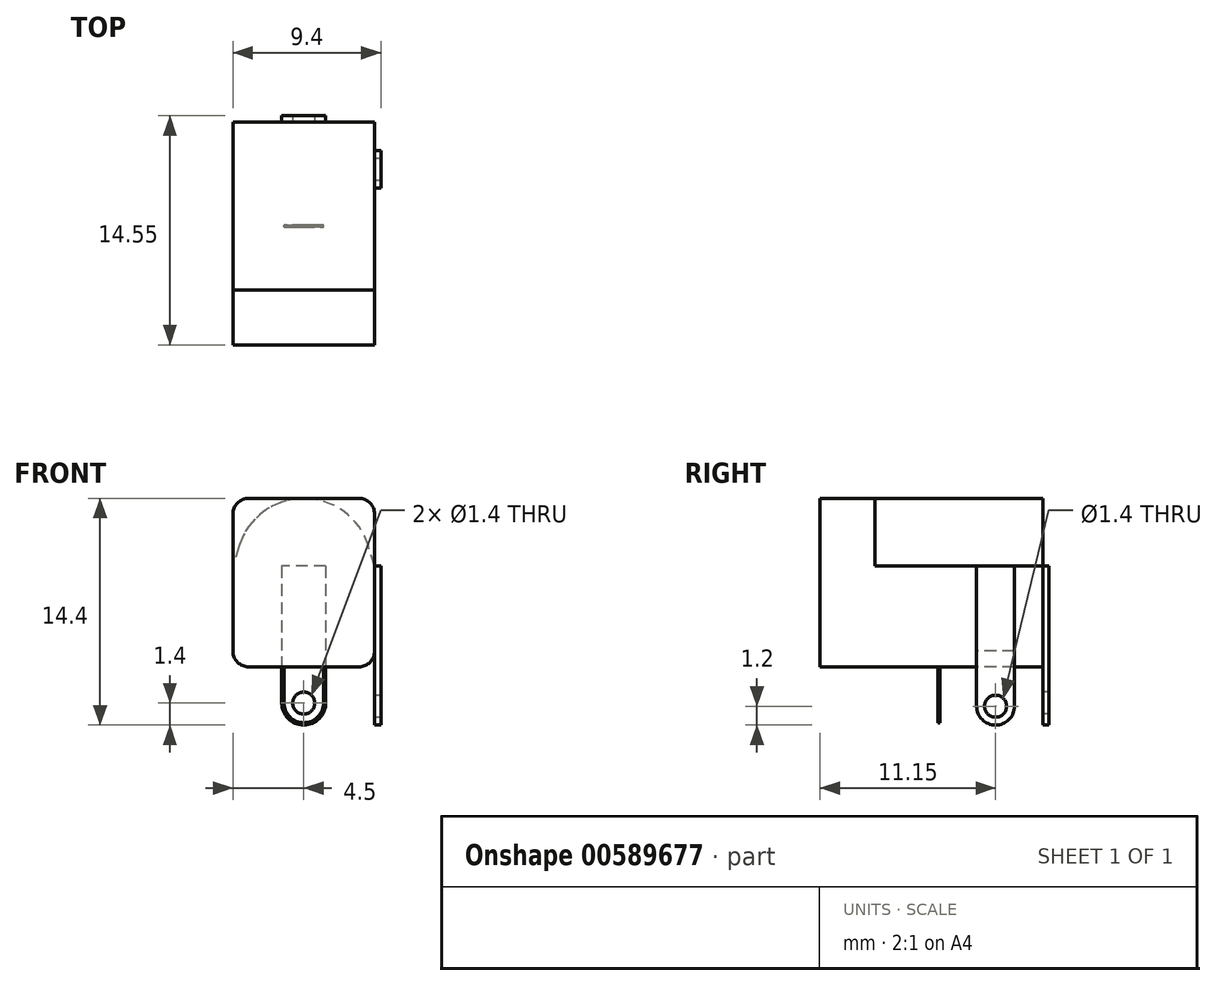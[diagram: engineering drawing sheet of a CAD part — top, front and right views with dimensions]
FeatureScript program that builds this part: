
annotation { "Feature Type Name" : "Feature", "Feature Type Description" : "" }
export const myFeature = defineFeature(function(context is Context, id is Id, definition is map)
    precondition{}
    {
        {
            var Q0;
            Q0=qCreatedBy(makeId("Front.planeOp"),FACE);
            var sketch = newSketch(context, id + "F0", { "sketchPlane" : qUnion([Q0])});
            skArc(sketch, "E0", {"start": v(-4.1, 1.27) * mm, "mid": v(0, 4.3) * mm, "end": v(4.1, 1.27) * mm});
            skLineSegment(sketch, "E1", {"start": v(-4.5, 0) * mm, "end": v(-4.5, -6.4) * mm});
            skLineSegment(sketch, "E2", {"start": v(4.5, -6.4) * mm, "end": v(4.5, 0) * mm});
            skLineSegment(sketch, "E3", {"start": v(-4.5, -6.4) * mm, "end": v(0, -6.4) * mm});
            skLineSegment(sketch, "E4", {"start": v(4.5, -6.4) * mm, "end": v(0, -6.4) * mm});
            skLineSegment(sketch, "E5", {"start": v(-4.1, 1.27) * mm, "end": v(-4.5, 0) * mm});
            skLineSegment(sketch, "E6", {"start": v(4.5, 0) * mm, "end": v(4.1, 1.27) * mm});
            skSolve(sketch);
        }
        {
            var Q0;
            Q0 = qSketchRegion(id + "F0", true);
            extrude(context, id + "F1", {"entities" : qUnion([Q0]), "oppositeDirection" : true, "depth" : 10.65 * mm, "offsetDistance" : 25 * mm});
        }
        {
            var Q0;
            Q0=makeQuery(id+"F1.opExtrude","CAP_FACE",FACE,{"disambiguationData":[OSD([sQuery(id+"F0.wireOp",EDGE,"E0"),sQuery(id+"F0.wireOp",EDGE,"12mtKoaY-uexj-lE4E-1jDO-Tng2IM5nw96I"),sQuery(id+"F0.wireOp",EDGE,"3pSl3QuJ-WNMO-4X7s-S6yP-eGF49RuyVbIp"),sQuery(id+"F0.wireOp",EDGE,"BtOXgUHt-va6U-RdGR-t7Iu-fnoyt6HXPqQ7")])],"isStart":true});
            var sketch = newSketch(context, id + "F2", { "sketchPlane" : qUnion([Q0])});
            skLineSegment(sketch, "E7.bottom", {"start": v(-4.5, -6.4) * mm, "end": v(4.5, -6.4) * mm});
            skLineSegment(sketch, "E7.top", {"start": v(-4.5, 4.3) * mm, "end": v(4.5, 4.3) * mm});
            skLineSegment(sketch, "E7.left", {"start": v(-4.5, -6.4) * mm, "end": v(-4.5, 4.3) * mm});
            skLineSegment(sketch, "E7.right", {"start": v(4.5, -6.4) * mm, "end": v(4.5, 4.3) * mm});
            skSolve(sketch);
        }
        {
            var Q0;
            Q0 = qSketchRegion(id + "F2", true);
            extrude(context, id + "F3", {"entities" : qUnion([Q0]), "operationType" : NewBodyOperationType.ADD, "depth" : 3.5 * mm, "offsetDistance" : 25 * mm});
        }
        {
            var Q0;
            Q0=makeQuery(id+"F3.opExtrude","SWEPT_EDGE",EDGE,{"disambiguationData":[OSD([sQuery(id+"F2.wireOp",EDGE,"E7.top"),sQuery(id+"F2.wireOp",EDGE,"E7.right")])]});
            var Q1;
            Q1=makeQuery(id+"F3.opExtrude","SWEPT_EDGE",EDGE,{"disambiguationData":[OSD([sQuery(id+"F2.wireOp",EDGE,"E7.top"),sQuery(id+"F2.wireOp",EDGE,"E7.left")])]});
            var Q2;
            Q2=makeQuery(id+"F3.boolean.opBoolean","MERGE",EDGE,{"derivedFrom":[makeQuery(id+"F1.opExtrude","SWEPT_EDGE",EDGE,{"disambiguationData":[OSD([sQuery(id+"F0.wireOp",EDGE,"E2"),sQuery(id+"F0.wireOp",EDGE,"E4")])]}),makeQuery(id+"F3.opExtrude","SWEPT_EDGE",EDGE,{"disambiguationData":[OSD([sQuery(id+"F2.wireOp",EDGE,"E7.bottom"),sQuery(id+"F2.wireOp",EDGE,"E7.right")])]})]});
            var Q3;
            Q3=makeQuery(id+"F3.boolean.opBoolean","MERGE",EDGE,{"derivedFrom":[makeQuery(id+"F1.opExtrude","SWEPT_EDGE",EDGE,{"disambiguationData":[OSD([sQuery(id+"F0.wireOp",EDGE,"E1"),sQuery(id+"F0.wireOp",EDGE,"E3")])]}),makeQuery(id+"F3.opExtrude","SWEPT_EDGE",EDGE,{"disambiguationData":[OSD([sQuery(id+"F2.wireOp",EDGE,"E7.bottom"),sQuery(id+"F2.wireOp",EDGE,"E7.left")])]})]});
            fillet(context, id + "F4", {"entities" : qUnion([Q0, Q1, Q2, Q3]), "radius" : 1 * mm, "tangentPropagation" : true, "allowEdgeOverflow" : false});
        }
        {
            var Q0;
            Q0=makeQuery(id+"F3.boolean.opBoolean","MERGE",FACE,{"derivedFrom":[makeQuery(id+"F1.opExtrude","SWEPT_FACE",FACE,{"disambiguationData":[OSD([sQuery(id+"F0.wireOp",EDGE,"E2")])]}),makeQuery(id+"F3.opExtrude","SWEPT_FACE",FACE,{"disambiguationData":[OSD([sQuery(id+"F2.wireOp",EDGE,"E7.right")])]})]});
            var sketch = newSketch(context, id + "F5", { "sketchPlane" : qUnion([Q0])});
            skArc(sketch, "E8", {"start": v(8.85, -8.9) * mm, "mid": v(7.65, -10.1) * mm, "end": v(6.45, -8.9) * mm});
            skLineSegment(sketch, "E9", {"start": v(6.45, 0) * mm, "end": v(8.85, 0) * mm});
            skLineSegment(sketch, "E10", {"start": v(8.85, 0) * mm, "end": v(8.85, -8.9) * mm});
            skLineSegment(sketch, "E11", {"start": v(6.45, 0) * mm, "end": v(6.45, -8.9) * mm});
            skCircle(sketch, "E12", {"center": v(7.65, -8.9) * mm, "radius": 0.7 * mm});
            skLineSegment(sketch, "E13", {"start": v(6.45, -8.9) * mm, "end": v(7.65, -8.9) * mm, "construction": true});
            skLineSegment(sketch, "E14", {"start": v(7.65, -8.9) * mm, "end": v(8.85, -8.9) * mm, "construction": true});
            skSolve(sketch);
        }
        {
            var Q0;
            Q0 = qSketchRegion(id + "F5", true);
            extrude(context, id + "F6", {"entities" : qUnion([Q0]), "operationType" : NewBodyOperationType.ADD, "depth" : 0.4 * mm, "offsetDistance" : 25 * mm});
        }
        {
            var Q0;
            Q0=makeQuery(id+"F1.opExtrude","CAP_FACE",FACE,{"disambiguationData":[OSD([sQuery(id+"F0.wireOp",EDGE,"E0"),sQuery(id+"F0.wireOp",EDGE,"E1"),sQuery(id+"F0.wireOp",EDGE,"E2"),sQuery(id+"F0.wireOp",EDGE,"E3"),sQuery(id+"F0.wireOp",EDGE,"E4"),sQuery(id+"F0.wireOp",EDGE,"E5"),sQuery(id+"F0.wireOp",EDGE,"E6")])],"isStart":false});
            var sketch = newSketch(context, id + "F7", { "sketchPlane" : qUnion([Q0])});
            skArc(sketch, "E15", {"start": v(1.4, -8.7) * mm, "mid": v(0, -10.1) * mm, "end": v(-1.4, -8.7) * mm});
            skLineSegment(sketch, "E16", {"start": v(-1.4, 0) * mm, "end": v(1.4, 0) * mm});
            skLineSegment(sketch, "E17", {"start": v(1.4, 0) * mm, "end": v(1.4, -8.7) * mm});
            skLineSegment(sketch, "E18", {"start": v(-1.4, 0) * mm, "end": v(-1.4, -8.7) * mm});
            skCircle(sketch, "E19", {"center": v(0, -8.7) * mm, "radius": 0.7 * mm});
            skLineSegment(sketch, "E20", {"start": v(0, -10.1) * mm, "end": v(-4.5, -10.1) * mm, "construction": true});
            skLineSegment(sketch, "E21", {"start": v(0, -8.7) * mm, "end": v(0, -10.1) * mm, "construction": true});
            skLineSegment(sketch, "E22", {"start": v(-1.4, -8.7) * mm, "end": v(1.4, -8.7) * mm, "construction": true});
            skSolve(sketch);
        }
        {
            var Q0;
            Q0 = qSketchRegion(id + "F7", true);
            extrude(context, id + "F8", {"entities" : qUnion([Q0]), "operationType" : NewBodyOperationType.ADD, "depth" : 0.4 * mm, "offsetDistance" : 25 * mm});
        }
        {
            var Q0;
            Q0=makeQuery(id+"F3.opExtrude","CAP_FACE",FACE,{"disambiguationData":[OSD([sQuery(id+"F2.wireOp",EDGE,"E7.bottom"),sQuery(id+"F2.wireOp",EDGE,"E7.top"),sQuery(id+"F2.wireOp",EDGE,"E7.left"),sQuery(id+"F2.wireOp",EDGE,"E7.right")])],"isStart":false});
            cPlane(context, id + "F9", {"entities" : qUnion([Q0]), "cplaneType" : CPlaneType.OFFSET, "offset" : 7.55 * mm, "oppositeDirection" : true, "width" : 150 * mm, "height" : 150 * mm});
        }
        {
            var Q0;
            Q0=qCreatedBy(id+"F9.planeOp",FACE);
            var sketch = newSketch(context, id + "F10", { "sketchPlane" : qUnion([Q0])});
            skArc(sketch, "E23", {"start": v(1.25, -8.7) * mm, "mid": v(0, -9.95) * mm, "end": v(-1.25, -8.7) * mm});
            skLineSegment(sketch, "E24", {"start": v(-1.25, 0) * mm, "end": v(1.25, 0) * mm});
            skLineSegment(sketch, "E25", {"start": v(1.25, 0) * mm, "end": v(1.25, -8.7) * mm});
            skLineSegment(sketch, "E26", {"start": v(-1.25, 0) * mm, "end": v(-1.25, -8.7) * mm});
            skCircle(sketch, "E27", {"center": v(0, -8.7) * mm, "radius": 0.7 * mm});
            skLineSegment(sketch, "E28", {"start": v(0, -8.7) * mm, "end": v(0, -9.95) * mm, "construction": true});
            skLineSegment(sketch, "E29", {"start": v(-1.25, -8.7) * mm, "end": v(1.25, -8.7) * mm, "construction": true});
            skSolve(sketch);
        }
        {
            var Q0;
            Q0 = qSketchRegion(id + "F10", true);
            extrude(context, id + "F11", {"entities" : qUnion([Q0]), "operationType" : NewBodyOperationType.ADD, "endBound" : BoundingType.SYMMETRIC, "oppositeDirection" : true, "depth" : 0.1 * mm, "offsetDistance" : 25 * mm});
        }
        {
            var Q0;
            Q0=makeQuery(id+"F8.opExtrude","CAP_FACE",FACE,{"disambiguationData":[OSD([sQuery(id+"F7.wireOp",EDGE,"E15"),sQuery(id+"F7.wireOp",EDGE,"E16"),sQuery(id+"F7.wireOp",EDGE,"E17"),sQuery(id+"F7.wireOp",EDGE,"E18"),sQuery(id+"F7.wireOp",EDGE,"E19")])],"isStart":false});
            var sketch = newSketch(context, id + "F12", { "sketchPlane" : qUnion([Q0])});
            skPoint(sketch, "E30", {"position": v(0, -8.7) * mm});
            skSolve(sketch);
        }
        {
            var Q0;
            Q0=makeQuery(id+"F3.boolean.opBoolean","MERGE",FACE,{"derivedFrom":[makeQuery(id+"F1.opExtrude","SWEPT_FACE",FACE,{"disambiguationData":[OSD([sQuery(id+"F0.wireOp",EDGE,"E3"),sQuery(id+"F0.wireOp",EDGE,"E4")])]}),makeQuery(id+"F3.opExtrude","SWEPT_FACE",FACE,{"disambiguationData":[OSD([sQuery(id+"F2.wireOp",EDGE,"E7.bottom")])]})]});
            var Q1;
            Q1=sQuery(id+"F12.wireOp",VERTEX,"E30");
            cPlane(context, id + "F13", {"entities" : qUnion([Q0, Q1]), "cplaneType" : CPlaneType.PLANE_POINT, "offset" : 25 * mm, "width" : 150 * mm, "height" : 150 * mm});
        }
        {
            var Q0;
            Q0=qCreatedBy(id+"F13.planeOp",FACE);
            var sketch = newSketch(context, id + "F14", { "sketchPlane" : qUnion([Q0])});
            skLineSegment(sketch, "E31", {"start": v(0, -11.05) * mm, "end": v(0, -10.65) * mm, "construction": true});
            skPoint(sketch, "E32", {"position": v(0, -10.85) * mm});
            skSolve(sketch);
        }
        {
            var Q0;
            Q0=makeQuery(id+"F6.opExtrude","CAP_FACE",FACE,{"disambiguationData":[OSD([sQuery(id+"F5.wireOp",EDGE,"E8"),sQuery(id+"F5.wireOp",EDGE,"E9"),sQuery(id+"F5.wireOp",EDGE,"E10"),sQuery(id+"F5.wireOp",EDGE,"E11"),sQuery(id+"F5.wireOp",EDGE,"E12")])],"isStart":false});
            var sketch = newSketch(context, id + "F15", { "sketchPlane" : qUnion([Q0])});
            skPoint(sketch, "E33", {"position": v(7.65, -8.9) * mm});
            skSolve(sketch);
        }
        {
            var Q0;
            Q0=makeQuery(id+"F3.boolean.opBoolean","MERGE",FACE,{"derivedFrom":[makeQuery(id+"F1.opExtrude","SWEPT_FACE",FACE,{"disambiguationData":[OSD([sQuery(id+"F0.wireOp",EDGE,"E3"),sQuery(id+"F0.wireOp",EDGE,"E4")])]}),makeQuery(id+"F3.opExtrude","SWEPT_FACE",FACE,{"disambiguationData":[OSD([sQuery(id+"F2.wireOp",EDGE,"E7.bottom")])]})]});
            var Q1;
            Q1=sQuery(id+"F15.wireOp",VERTEX,"E33");
            cPlane(context, id + "F16", {"entities" : qUnion([Q0, Q1]), "cplaneType" : CPlaneType.PLANE_POINT, "offset" : 25 * mm, "width" : 150 * mm, "height" : 150 * mm});
        }
        {
            var Q0;
            Q0=qCreatedBy(id+"F16.planeOp",FACE);
            var sketch = newSketch(context, id + "F17", { "sketchPlane" : qUnion([Q0])});
            skLineSegment(sketch, "E34", {"start": v(4.9, -7.65) * mm, "end": v(4.5, -7.65) * mm, "construction": true});
            skPoint(sketch, "E35", {"position": v(4.7, -7.65) * mm});
            skSolve(sketch);
        }
    });
